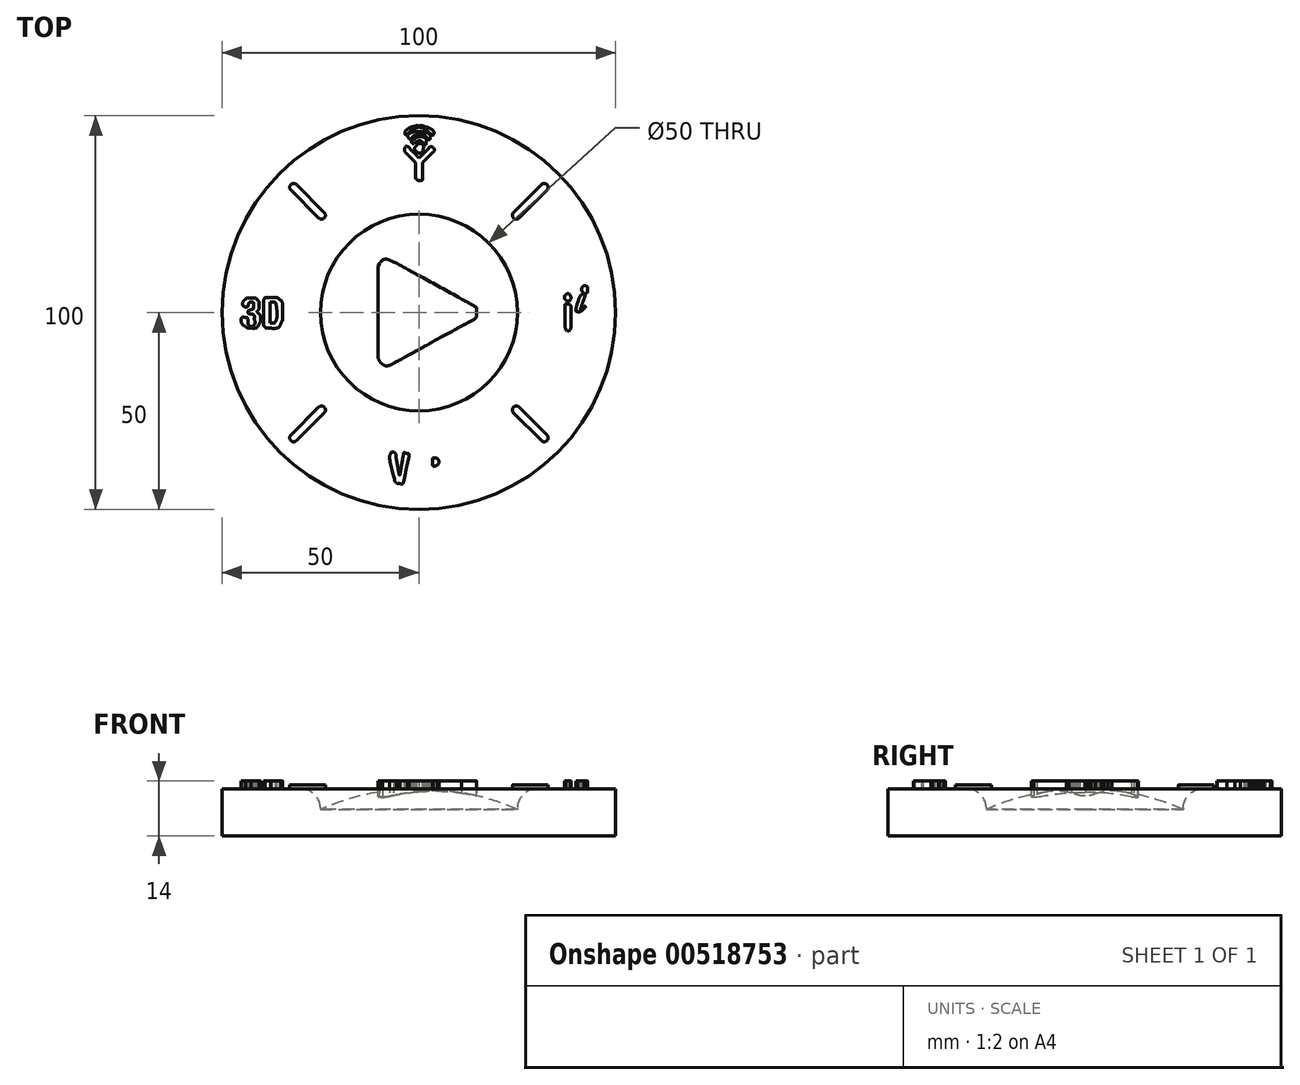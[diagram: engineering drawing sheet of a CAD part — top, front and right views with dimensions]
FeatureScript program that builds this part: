
annotation { "Feature Type Name" : "Feature", "Feature Type Description" : "" }
export const myFeature = defineFeature(function(context is Context, id is Id, definition is map)
    precondition{}
    {
        {
            var Q0;
            Q0=qCreatedBy(makeId("Top.planeOp"),FACE);
            var sketch = newSketch(context, id + "F0", { "sketchPlane" : qUnion([Q0])});
            skCircle(sketch, "E0", {"center": v(0, 0) * mm, "radius": 50 * mm});
            skCircle(sketch, "E1", {"center": v(0, 0) * mm, "radius": 25 * mm});
            skSolve(sketch);
        }
        {
            var Q0;
            Q0=makeQuery(id+"F0.imprint","IMPRINT",FACE,{"disambiguationData":[TD([[makeQuery(id+"F0.imprint","IMPRINT",EDGE,{"derivedFrom":sQuery(id+"F0.wireOp",EDGE,"E0")}),1.0]])]});
            extrude(context, id + "F1", {"entities" : qUnion([Q0]), "depth" : 25 * mm, "offsetDistance" : 25 * mm});
        }
        {
            var Q0;
            Q0=qCreatedBy(makeId("Front.planeOp"),FACE);
            var sketch = newSketch(context, id + "F2", { "sketchPlane" : qUnion([Q0])});
            skLineSegment(sketch, "E2", {"start": v(-50, 0) * mm, "end": v(50, 0) * mm});
            skLineSegment(sketch, "E3", {"start": v(0, 25) * mm, "end": v(0, 0) * mm});
            skArc(sketch, "E4", {"start": v(50, 0) * mm, "mid": v(27.95, 18.4) * mm, "end": v(0, 25) * mm});
            skLineSegment(sketch, "E5", {"start": v(0, 0) * mm, "end": v(0, -37.5) * mm});
            skSolve(sketch);
        }
        {
            var Q0;
            Q0 = qSketchRegion(id + "F2", true);
            var Q1;
            Q1=sQuery(id+"F2.wireOp",EDGE,"E3");
            revolve(context, id + "F3", {"operationType" : NewBodyOperationType.ADD, "entities" : qUnion([Q0]), "axis" : qUnion([Q1]), "revolveType" : RevolveType.FULL});
        }
        {
            var Q0;
            Q0=makeQuery(id+"F1.opExtrude","CAP_EDGE",EDGE,{"disambiguationData":[OSD([sQuery(id+"F0.wireOp",EDGE,"E1")])],"isStart":false});
            fillet(context, id + "F4", {"entities" : qUnion([Q0]), "radius" : 5 * mm, "tangentPropagation" : true, "allowEdgeOverflow" : false});
        }
        {
            var Q0;
            Q0=makeQuery(id+"F1.opExtrude","CAP_FACE",FACE,{"disambiguationData":[OSD([sQuery(id+"F0.wireOp",EDGE,"E0"),sQuery(id+"F0.wireOp",EDGE,"E1")])],"isStart":false});
            var sketch = newSketch(context, id + "F5", { "sketchPlane" : qUnion([Q0])});
            skLineSegment(sketch, "E6", {"start": v(-24.75, 24.75) * mm, "end": v(-31.82, 31.82) * mm, "construction": true});
            skLineSegment(sketch, "E7", {"start": v(24.75, -24.75) * mm, "end": v(31.82, -31.82) * mm, "construction": true});
            skLineSegment(sketch, "E8", {"start": v(31.82, 31.82) * mm, "end": v(24.75, 24.75) * mm, "construction": true});
            skLineSegment(sketch, "E9", {"start": v(-24.75, -24.75) * mm, "end": v(-31.82, -31.82) * mm, "construction": true});
            skCircle(sketch, "E10", {"center": v(0, 0) * mm, "radius": 35 * mm, "construction": true});
            skCircle(sketch, "E11", {"center": v(0, 0) * mm, "radius": 45 * mm, "construction": true});
            skArc(sketch, "E12", {"start": v(-25.46, 24.04) * mm, "mid": v(-24.04, 24.04) * mm, "end": v(-24.04, 25.46) * mm});
            skArc(sketch, "E13", {"start": v(-31.1, 32.52) * mm, "mid": v(-32.53, 32.53) * mm, "end": v(-32.52, 31.1) * mm});
            skLineSegment(sketch, "E14", {"start": v(-31.11, 32.53) * mm, "end": v(-24.04, 25.46) * mm});
            skLineSegment(sketch, "E15", {"start": v(-32.53, 31.11) * mm, "end": v(-25.46, 24.04) * mm});
            skArc(sketch, "E16", {"start": v(32.52, 31.1) * mm, "mid": v(32.53, 32.53) * mm, "end": v(31.1, 32.52) * mm});
            skArc(sketch, "E17", {"start": v(24.04, 25.46) * mm, "mid": v(24.04, 24.04) * mm, "end": v(25.46, 24.04) * mm});
            skLineSegment(sketch, "E18", {"start": v(32.53, 31.11) * mm, "end": v(25.46, 24.04) * mm});
            skLineSegment(sketch, "E19", {"start": v(31.11, 32.53) * mm, "end": v(24.04, 25.46) * mm});
            skArc(sketch, "E20", {"start": v(25.46, -24.04) * mm, "mid": v(24.04, -24.04) * mm, "end": v(24.04, -25.46) * mm});
            skArc(sketch, "E21", {"start": v(31.1, -32.52) * mm, "mid": v(32.53, -32.53) * mm, "end": v(32.52, -31.1) * mm});
            skLineSegment(sketch, "E22", {"start": v(25.46, -24.04) * mm, "end": v(32.53, -31.11) * mm});
            skLineSegment(sketch, "E23", {"start": v(24.04, -25.46) * mm, "end": v(31.11, -32.53) * mm});
            skArc(sketch, "E24", {"start": v(-24.04, -25.46) * mm, "mid": v(-24.04, -24.04) * mm, "end": v(-25.46, -24.04) * mm});
            skArc(sketch, "E25", {"start": v(-32.52, -31.1) * mm, "mid": v(-32.53, -32.53) * mm, "end": v(-31.1, -32.52) * mm});
            skLineSegment(sketch, "E26", {"start": v(-32.53, -31.11) * mm, "end": v(-25.46, -24.04) * mm});
            skLineSegment(sketch, "E27", {"start": v(-24.04, -25.46) * mm, "end": v(-31.11, -32.53) * mm});
            skSolve(sketch);
        }
        {
            var Q0;
            Q0 = qSketchRegion(id + "F5", true);
            extrude(context, id + "F6", {"entities" : qUnion([Q0]), "operationType" : NewBodyOperationType.ADD, "depth" : 1 * mm, "offsetDistance" : 25 * mm});
        }
        {
            var Q0;
            Q0=makeQuery(id+"F1.opExtrude","CAP_FACE",FACE,{"disambiguationData":[OSD([sQuery(id+"F0.wireOp",EDGE,"E0"),sQuery(id+"F0.wireOp",EDGE,"E1")])],"isStart":false});
            var sketch = newSketch(context, id + "F7", { "sketchPlane" : qUnion([Q0])});
            skFitSpline(sketch, "E28", {"points": [v(-1.16, -44.63) * mm, v(-1.22, -44.57) * mm, v(-1.27, -44.21) * mm, v(-1.27, -43.84) * mm]});
            skFitSpline(sketch, "E29", {"points": [v(-1.98, -43.15) * mm, v(-2.6, -43.15) * mm, v(-2.7, -43.1) * mm, v(-2.7, -42.83) * mm]});
            skFitSpline(sketch, "E30", {"points": [v(-2.7, -42.83) * mm, v(-2.7, -42.56) * mm, v(-2.6, -42.51) * mm, v(-2, -42.51) * mm]});
            skLineSegment(sketch, "E31", {"start": v(-1.27, -43.84) * mm, "end": v(-1.27, -43.15) * mm});
            skLineSegment(sketch, "E32", {"start": v(-1.27, -43.15) * mm, "end": v(-1.98, -43.15) * mm});
            skFitSpline(sketch, "E33", {"points": [v(-1.24, -41.76) * mm, v(-1.2, -41.13) * mm, v(-1.14, -41) * mm, v(-0.87, -41) * mm]});
            skFitSpline(sketch, "E34", {"points": [v(-0.87, -41) * mm, v(-0.6, -41) * mm, v(-0.55, -41.13) * mm, v(-0.5, -41.76) * mm]});
            skLineSegment(sketch, "E35", {"start": v(-2, -42.51) * mm, "end": v(-1.28, -42.51) * mm});
            skLineSegment(sketch, "E36", {"start": v(-1.28, -42.51) * mm, "end": v(-1.24, -41.76) * mm});
            skFitSpline(sketch, "E37", {"points": [v(0.25, -42.51) * mm, v(0.85, -42.51) * mm, v(0.95, -42.56) * mm, v(0.95, -42.83) * mm]});
            skFitSpline(sketch, "E38", {"points": [v(0.95, -42.83) * mm, v(0.95, -43.1) * mm, v(0.85, -43.15) * mm, v(0.24, -43.15) * mm]});
            skLineSegment(sketch, "E39", {"start": v(-0.5, -41.76) * mm, "end": v(-0.46, -42.51) * mm});
            skLineSegment(sketch, "E40", {"start": v(-0.46, -42.51) * mm, "end": v(0.25, -42.51) * mm});
            skFitSpline(sketch, "E41", {"points": [v(-0.47, -43.84) * mm, v(-0.47, -44.33) * mm, v(-0.55, -44.57) * mm, v(-0.72, -44.64) * mm]});
            skFitSpline(sketch, "E42", {"points": [v(-0.72, -44.64) * mm, v(-1.04, -44.76) * mm, v(-1.03, -44.76) * mm, v(-1.16, -44.63) * mm]});
            skLineSegment(sketch, "E43", {"start": v(0.24, -43.15) * mm, "end": v(-0.47, -43.15) * mm});
            skLineSegment(sketch, "E44", {"start": v(-0.47, -43.15) * mm, "end": v(-0.47, -43.84) * mm});
            skFitSpline(sketch, "E45", {"points": [v(-5.73, -43.2) * mm, v(-6.06, -42.81) * mm, v(-7.46, -36.46) * mm, v(-7.29, -36.14) * mm]});
            skFitSpline(sketch, "E46", {"points": [v(-7.29, -36.14) * mm, v(-6.91, -35.44) * mm, v(-5.98, -35.78) * mm, v(-5.82, -36.67) * mm]});
            skFitSpline(sketch, "E47", {"points": [v(-5.82, -36.67) * mm, v(-5.43, -38.9) * mm, v(-5.05, -40.9) * mm, v(-4.96, -41.16) * mm]});
            skFitSpline(sketch, "E48", {"points": [v(-4.96, -41.16) * mm, v(-4.9, -41.35) * mm, v(-4.71, -40.6) * mm, v(-4.49, -39.26) * mm]});
            skFitSpline(sketch, "E49", {"points": [v(-4.49, -39.26) * mm, v(-3.9, -35.79) * mm, v(-3.82, -35.59) * mm, v(-3.03, -35.8) * mm]});
            skFitSpline(sketch, "E50", {"points": [v(-3.03, -35.8) * mm, v(-2.53, -35.93) * mm, v(-2.49, -36.41) * mm, v(-2.84, -38) * mm]});
            skFitSpline(sketch, "E51", {"points": [v(-2.84, -38) * mm, v(-3.01, -38.78) * mm, v(-3.3, -40.17) * mm, v(-3.5, -41.08) * mm]});
            skFitSpline(sketch, "E52", {"points": [v(-3.5, -41.08) * mm, v(-3.92, -43.17) * mm, v(-4.1, -43.46) * mm, v(-4.9, -43.46) * mm]});
            skFitSpline(sketch, "E53", {"points": [v(-4.9, -43.46) * mm, v(-5.28, -43.46) * mm, v(-5.6, -43.36) * mm, v(-5.73, -43.2) * mm]});
            skFitSpline(sketch, "E54", {"points": [v(2.26, -43.27) * mm, v(2.12, -43.14) * mm, v(2.07, -42.09) * mm, v(2.07, -39.55) * mm]});
            skFitSpline(sketch, "E55", {"points": [v(2.07, -39.55) * mm, v(2.07, -35.44) * mm, v(1.95, -35.69) * mm, v(3.84, -35.69) * mm]});
            skFitSpline(sketch, "E56", {"points": [v(3.84, -35.69) * mm, v(5.74, -35.69) * mm, v(6.5, -36.27) * mm, v(6.5, -37.72) * mm]});
            skFitSpline(sketch, "E57", {"points": [v(6.5, -37.72) * mm, v(6.51, -38.45) * mm, v(6.14, -39.34) * mm, v(5.84, -39.34) * mm]});
            skFitSpline(sketch, "E58", {"points": [v(5.84, -39.34) * mm, v(5.74, -39.34) * mm, v(5.81, -39.48) * mm, v(6, -39.66) * mm]});
            skFitSpline(sketch, "E59", {"points": [v(6, -39.66) * mm, v(6.46, -40.09) * mm, v(6.53, -40.44) * mm, v(6.48, -42.04) * mm]});
            skFitSpline(sketch, "E60", {"points": [v(5.88, -43.44) * mm, v(5.12, -43.5) * mm, v(4.92, -43.18) * mm, v(4.92, -41.84) * mm]});
            skFitSpline(sketch, "E61", {"points": [v(4.92, -41.84) * mm, v(4.92, -40.45) * mm, v(4.76, -40.13) * mm, v(4.04, -40.13) * mm]});
            skLineSegment(sketch, "E62", {"start": v(6.48, -42.04) * mm, "end": v(6.43, -43.39) * mm});
            skLineSegment(sketch, "E63", {"start": v(6.43, -43.39) * mm, "end": v(5.88, -43.44) * mm});
            skFitSpline(sketch, "E64", {"points": [v(3.5, -41.6) * mm, v(3.5, -43.16) * mm, v(3.38, -43.46) * mm, v(2.78, -43.46) * mm]});
            skFitSpline(sketch, "E65", {"points": [v(2.78, -43.46) * mm, v(2.6, -43.46) * mm, v(2.36, -43.38) * mm, v(2.26, -43.27) * mm]});
            skLineSegment(sketch, "E66", {"start": v(4.04, -40.13) * mm, "end": v(3.5, -40.13) * mm});
            skLineSegment(sketch, "E67", {"start": v(3.5, -40.13) * mm, "end": v(3.5, -41.6) * mm});
            skFitSpline(sketch, "E68", {"points": [v(4.72, -38.66) * mm, v(4.98, -38.46) * mm, v(4.98, -37.4) * mm, v(4.73, -37.15) * mm]});
            skFitSpline(sketch, "E69", {"points": [v(4.73, -37.15) * mm, v(4.63, -37.04) * mm, v(4.3, -36.96) * mm, v(4.02, -36.96) * mm]});
            skFitSpline(sketch, "E70", {"points": [v(3.5, -37.88) * mm, v(3.5, -38.4) * mm, v(3.54, -38.86) * mm, v(3.6, -38.91) * mm]});
            skFitSpline(sketch, "E71", {"points": [v(3.6, -38.91) * mm, v(3.72, -39.04) * mm, v(4.45, -38.88) * mm, v(4.72, -38.66) * mm]});
            skLineSegment(sketch, "E72", {"start": v(4.02, -36.96) * mm, "end": v(3.5, -36.96) * mm});
            skLineSegment(sketch, "E73", {"start": v(3.5, -36.96) * mm, "end": v(3.5, -37.88) * mm});
            skFitSpline(sketch, "E74", {"points": [v(-9.29, -13.06) * mm, v(-9.56, -12.9) * mm, v(-9.91, -12.49) * mm, v(-10.08, -12.15) * mm]});
            skFitSpline(sketch, "E75", {"points": [v(-10.08, -12.15) * mm, v(-10.37, -11.56) * mm, v(-10.39, -11.05) * mm, v(-10.39, 0.14) * mm]});
            skFitSpline(sketch, "E76", {"points": [v(-9.95, 12.48) * mm, v(-9.52, 13.12) * mm, v(-8.57, 13.59) * mm, v(-7.48, 13.3) * mm]});
            skFitSpline(sketch, "E77", {"points": [v(-7.48, 13.3) * mm, v(-7.08, 13.21) * mm, v(-3.83, 11.51) * mm, v(-0.24, 9.54) * mm]});
            skFitSpline(sketch, "E78", {"points": [v(-0.24, 9.54) * mm, v(3.35, 7.57) * mm, v(7.89, 5.07) * mm, v(9.85, 4) * mm]});
            skFitSpline(sketch, "E79", {"points": [v(9.85, 4) * mm, v(13.83, 1.81) * mm, v(14.61, 1.19) * mm, v(14.61, 0.2) * mm]});
            skFitSpline(sketch, "E80", {"points": [v(14.61, 0.2) * mm, v(14.61, -1.08) * mm, v(13.93, -1.73) * mm, v(10.8, -3.44) * mm]});
            skFitSpline(sketch, "E81", {"points": [v(10.8, -3.44) * mm, v(9.53, -4.12) * mm, v(5.34, -6.42) * mm, v(1.47, -8.55) * mm]});
            skFitSpline(sketch, "E82", {"points": [v(1.47, -8.55) * mm, v(-2.4, -10.68) * mm, v(-5.98, -12.63) * mm, v(-6.49, -12.9) * mm]});
            skFitSpline(sketch, "E83", {"points": [v(-6.49, -12.9) * mm, v(-7.58, -13.45) * mm, v(-8.56, -13.5) * mm, v(-9.29, -13.06) * mm]});
            skLineSegment(sketch, "E84", {"start": v(-10.39, 0.14) * mm, "end": v(-10.39, 11.82) * mm});
            skLineSegment(sketch, "E85", {"start": v(-10.39, 11.82) * mm, "end": v(-9.95, 12.48) * mm});
            skFitSpline(sketch, "E86", {"points": [v(-4.77, -10.48) * mm, v(-3.32, -9.68) * mm, v(-1.77, -8.84) * mm, v(-1.34, -8.6) * mm]});
            skFitSpline(sketch, "E87", {"points": [v(-1.34, -8.6) * mm, v(-0.9, -8.36) * mm, v(2.35, -6.58) * mm, v(5.88, -4.64) * mm]});
            skFitSpline(sketch, "E88", {"points": [v(5.88, -4.64) * mm, v(9.5, -2.67) * mm, v(12.5, -0.91) * mm, v(12.75, -0.65) * mm]});
            skFitSpline(sketch, "E89", {"points": [v(12.75, -0.65) * mm, v(13.28, -0.08) * mm, v(13.3, 0.29) * mm, v(12.83, 0.72) * mm]});
            skFitSpline(sketch, "E90", {"points": [v(12.83, 0.72) * mm, v(12.63, 0.9) * mm, v(10.3, 2.25) * mm, v(7.63, 3.7) * mm]});
            skFitSpline(sketch, "E91", {"points": [v(7.63, 3.7) * mm, v(4.97, 5.16) * mm, v(0.53, 7.6) * mm, v(-2.23, 9.12) * mm]});
            skFitSpline(sketch, "E92", {"points": [v(-2.23, 9.12) * mm, v(-6.44, 11.43) * mm, v(-7.35, 11.88) * mm, v(-7.9, 11.88) * mm]});
            skFitSpline(sketch, "E93", {"points": [v(-7.9, 11.88) * mm, v(-9.1, 11.88) * mm, v(-9.05, 12.42) * mm, v(-9, -0.07) * mm]});
            skFitSpline(sketch, "E94", {"points": [v(-9, -0.07) * mm, v(-8.96, -10.3) * mm, v(-8.94, -11.1) * mm, v(-8.68, -11.5) * mm]});
            skFitSpline(sketch, "E95", {"points": [v(-8.68, -11.5) * mm, v(-8.2, -12.22) * mm, v(-7.69, -12.09) * mm, v(-4.77, -10.48) * mm]});
            skFitSpline(sketch, "E96", {"points": [v(37.23, -3.98) * mm, v(37.14, -3.75) * mm, v(37.07, -2.47) * mm, v(37.07, -1.13) * mm]});
            skFitSpline(sketch, "E97", {"points": [v(37.07, -1.13) * mm, v(37.07, 1.7) * mm, v(37.18, 2.12) * mm, v(37.86, 2.12) * mm]});
            skFitSpline(sketch, "E98", {"points": [v(37.86, 2.12) * mm, v(38.17, 2.12) * mm, v(38.4, 2.01) * mm, v(38.5, 1.82) * mm]});
            skFitSpline(sketch, "E99", {"points": [v(38.5, 1.82) * mm, v(38.6, 1.64) * mm, v(38.66, 0.39) * mm, v(38.66, -1.13) * mm]});
            skFitSpline(sketch, "E100", {"points": [v(38.66, -1.13) * mm, v(38.66, -2.65) * mm, v(38.6, -3.9) * mm, v(38.5, -4.08) * mm]});
            skFitSpline(sketch, "E101", {"points": [v(38.5, -4.08) * mm, v(38.24, -4.56) * mm, v(37.43, -4.5) * mm, v(37.23, -3.98) * mm]});
            skFitSpline(sketch, "E102", {"points": [v(-44.03, -3.56) * mm, v(-44.99, -2.75) * mm, v(-45, -1.27) * mm, v(-44.06, -1.27) * mm]});
            skFitSpline(sketch, "E103", {"points": [v(-44.06, -1.27) * mm, v(-43.62, -1.27) * mm, v(-43.56, -1.33) * mm, v(-43.4, -1.98) * mm]});
            skFitSpline(sketch, "E104", {"points": [v(-43.4, -1.98) * mm, v(-43.01, -3.51) * mm, v(-41.83, -3.16) * mm, v(-41.83, -1.52) * mm]});
            skFitSpline(sketch, "E105", {"points": [v(-41.83, -1.52) * mm, v(-41.83, -0.84) * mm, v(-42.12, -0.47) * mm, v(-42.79, -0.33) * mm]});
            skFitSpline(sketch, "E106", {"points": [v(-42.79, -0.33) * mm, v(-43.23, -0.24) * mm, v(-43.33, -0.15) * mm, v(-43.33, 0.16) * mm]});
            skFitSpline(sketch, "E107", {"points": [v(-43.33, 0.16) * mm, v(-43.33, 0.44) * mm, v(-43.21, 0.57) * mm, v(-42.86, 0.69) * mm]});
            skFitSpline(sketch, "E108", {"points": [v(-42.86, 0.69) * mm, v(-42.14, 0.92) * mm, v(-41.99, 1.1) * mm, v(-41.99, 1.74) * mm]});
            skFitSpline(sketch, "E109", {"points": [v(-41.99, 1.74) * mm, v(-41.99, 2.4) * mm, v(-42.21, 2.7) * mm, v(-42.7, 2.7) * mm]});
            skFitSpline(sketch, "E110", {"points": [v(-42.7, 2.7) * mm, v(-42.96, 2.7) * mm, v(-43.11, 2.53) * mm, v(-43.3, 2.07) * mm]});
            skFitSpline(sketch, "E111", {"points": [v(-43.3, 2.07) * mm, v(-43.5, 1.57) * mm, v(-43.63, 1.43) * mm, v(-43.94, 1.43) * mm]});
            skFitSpline(sketch, "E112", {"points": [v(-43.94, 1.43) * mm, v(-44.15, 1.43) * mm, v(-44.42, 1.54) * mm, v(-44.52, 1.67) * mm]});
            skFitSpline(sketch, "E113", {"points": [v(-44.52, 1.67) * mm, v(-44.81, 2.01) * mm, v(-44.6, 2.9) * mm, v(-44.11, 3.35) * mm]});
            skFitSpline(sketch, "E114", {"points": [v(-44.11, 3.35) * mm, v(-43.76, 3.68) * mm, v(-43.55, 3.73) * mm, v(-42.6, 3.73) * mm]});
            skFitSpline(sketch, "E115", {"points": [v(-42.6, 3.73) * mm, v(-41.54, 3.73) * mm, v(-41.46, 3.7) * mm, v(-41.02, 3.22) * mm]});
            skFitSpline(sketch, "E116", {"points": [v(-41.02, 3.22) * mm, v(-40.63, 2.78) * mm, v(-40.56, 2.56) * mm, v(-40.56, 1.85) * mm]});
            skFitSpline(sketch, "E117", {"points": [v(-40.56, 1.85) * mm, v(-40.56, 1.24) * mm, v(-40.65, 0.88) * mm, v(-40.86, 0.62) * mm]});
            skFitSpline(sketch, "E118", {"points": [v(-40.86, 0.62) * mm, v(-41.17, 0.25) * mm, v(-41.16, 0.24) * mm, v(-40.83, -0.12) * mm]});
            skFitSpline(sketch, "E119", {"points": [v(-40.83, -0.12) * mm, v(-40.36, -0.63) * mm, v(-40.27, -2.23) * mm, v(-40.67, -3) * mm]});
            skFitSpline(sketch, "E120", {"points": [v(-40.67, -3) * mm, v(-41.04, -3.72) * mm, v(-41.53, -3.96) * mm, v(-42.65, -3.96) * mm]});
            skFitSpline(sketch, "E121", {"points": [v(-42.65, -3.96) * mm, v(-43.39, -3.96) * mm, v(-43.64, -3.89) * mm, v(-44.03, -3.56) * mm]});
            skFitSpline(sketch, "E122", {"points": [v(-39.13, -3.65) * mm, v(-39.43, -3.35) * mm, v(-39.45, -3.12) * mm, v(-39.45, -0.06) * mm]});
            skFitSpline(sketch, "E123", {"points": [v(-39.45, -0.06) * mm, v(-39.45, 1.88) * mm, v(-39.38, 3.32) * mm, v(-39.28, 3.5) * mm]});
            skFitSpline(sketch, "E124", {"points": [v(-39.28, 3.5) * mm, v(-39.14, 3.78) * mm, v(-38.94, 3.81) * mm, v(-37.55, 3.81) * mm]});
            skFitSpline(sketch, "E125", {"points": [v(-37.55, 3.81) * mm, v(-36.1, 3.81) * mm, v(-35.94, 3.78) * mm, v(-35.5, 3.4) * mm]});
            skFitSpline(sketch, "E126", {"points": [v(-35.5, 3.4) * mm, v(-34.84, 2.85) * mm, v(-34.63, 2.02) * mm, v(-34.63, -0.09) * mm]});
            skFitSpline(sketch, "E127", {"points": [v(-34.63, -0.09) * mm, v(-34.62, -1.64) * mm, v(-34.67, -1.94) * mm, v(-35.01, -2.63) * mm]});
            skFitSpline(sketch, "E128", {"points": [v(-35.01, -2.63) * mm, v(-35.52, -3.66) * mm, v(-36.13, -3.96) * mm, v(-37.66, -3.96) * mm]});
            skFitSpline(sketch, "E129", {"points": [v(-37.66, -3.96) * mm, v(-38.6, -3.96) * mm, v(-38.87, -3.9) * mm, v(-39.13, -3.65) * mm]});
            skFitSpline(sketch, "E130", {"points": [v(-36.52, -2.33) * mm, v(-36.22, -1.87) * mm, v(-36.04, 0.01) * mm, v(-36.18, 1.19) * mm]});
            skFitSpline(sketch, "E131", {"points": [v(-36.18, 1.19) * mm, v(-36.32, 2.24) * mm, v(-36.68, 2.7) * mm, v(-37.38, 2.7) * mm]});
            skFitSpline(sketch, "E132", {"points": [v(-37.3, -2.7) * mm, v(-36.9, -2.7) * mm, v(-36.69, -2.6) * mm, v(-36.52, -2.33) * mm]});
            skLineSegment(sketch, "E133", {"start": v(-37.38, 2.7) * mm, "end": v(-37.86, 2.7) * mm});
            skLineSegment(sketch, "E134", {"start": v(-37.86, 2.7) * mm, "end": v(-37.86, 0) * mm});
            skLineSegment(sketch, "E135", {"start": v(-37.86, 0) * mm, "end": v(-37.86, -2.7) * mm});
            skLineSegment(sketch, "E136", {"start": v(-37.86, -2.7) * mm, "end": v(-37.3, -2.7) * mm});
            skFitSpline(sketch, "E137", {"points": [v(39.93, 0.58) * mm, v(39.93, 1.1) * mm, v(41.03, 4.3) * mm, v(41.28, 4.5) * mm]});
            skFitSpline(sketch, "E138", {"points": [v(41.28, 4.5) * mm, v(41.5, 4.7) * mm, v(42.15, 4.47) * mm, v(42.15, 4.2) * mm]});
            skFitSpline(sketch, "E139", {"points": [v(42.15, 4.2) * mm, v(42.15, 4.14) * mm, v(41.94, 3.46) * mm, v(41.68, 2.7) * mm]});
            skFitSpline(sketch, "E140", {"points": [v(41.68, 2.7) * mm, v(41.07, 0.96) * mm, v(41.06, 0.66) * mm, v(41.6, 1.17) * mm]});
            skFitSpline(sketch, "E141", {"points": [v(41.6, 1.17) * mm, v(42.07, 1.62) * mm, v(42.33, 1.47) * mm, v(41.9, 1) * mm]});
            skFitSpline(sketch, "E142", {"points": [v(41.9, 1) * mm, v(41.5, 0.55) * mm, v(40.83, 0.22) * mm, v(40.34, 0.22) * mm]});
            skFitSpline(sketch, "E143", {"points": [v(40.34, 0.22) * mm, v(40.02, 0.22) * mm, v(39.93, 0.3) * mm, v(39.93, 0.58) * mm]});
            skFitSpline(sketch, "E144", {"points": [v(37.27, 3.26) * mm, v(37, 3.53) * mm, v(37.01, 4.21) * mm, v(37.3, 4.5) * mm]});
            skFitSpline(sketch, "E145", {"points": [v(37.3, 4.5) * mm, v(37.63, 4.77) * mm, v(38.22, 4.7) * mm, v(38.47, 4.34) * mm]});
            skFitSpline(sketch, "E146", {"points": [v(38.47, 4.34) * mm, v(38.57, 4.1) * mm, v(38.66, 3.75) * mm, v(38.5, 3.43) * mm]});
            skFitSpline(sketch, "E147", {"points": [v(38.5, 3.43) * mm, v(38.28, 2.98) * mm, v(37.6, 2.93) * mm, v(37.27, 3.26) * mm]});
            skFitSpline(sketch, "E148", {"points": [v(41.45, 5.49) * mm, v(41.24, 5.79) * mm, v(41.24, 5.89) * mm, v(41.42, 6.16) * mm]});
            skFitSpline(sketch, "E149", {"points": [v(41.42, 6.16) * mm, v(41.84, 6.8) * mm, v(42.79, 6.6) * mm, v(42.79, 5.87) * mm]});
            skFitSpline(sketch, "E150", {"points": [v(42.79, 5.87) * mm, v(42.79, 5.12) * mm, v(41.89, 4.87) * mm, v(41.45, 5.49) * mm]});
            skFitSpline(sketch, "E151", {"points": [v(-0.56, 33.85) * mm, v(-0.76, 34.05) * mm, v(-0.81, 34.5) * mm, v(-0.81, 36.12) * mm]});
            skFitSpline(sketch, "E152", {"points": [v(-2.24, 39.56) * mm, v(-3.14, 40.45) * mm, v(-3.67, 41.1) * mm, v(-3.67, 41.31) * mm]});
            skFitSpline(sketch, "E153", {"points": [v(-3.67, 41.31) * mm, v(-3.67, 41.64) * mm, v(-3.21, 42.26) * mm, v(-2.96, 42.17) * mm]});
            skFitSpline(sketch, "E154", {"points": [v(-2.96, 42.17) * mm, v(-2.54, 42.03) * mm, v(-2.18, 41.53) * mm, v(-1.38, 40.75) * mm]});
            skLineSegment(sketch, "E155", {"start": v(-0.81, 36.12) * mm, "end": v(-0.81, 38.13) * mm});
            skLineSegment(sketch, "E156", {"start": v(-0.81, 38.13) * mm, "end": v(-2.24, 39.56) * mm});
            skFitSpline(sketch, "E157", {"points": [v(1.41, 40.67) * mm, v(2.74, 42) * mm, v(3.19, 42.24) * mm, v(3.6, 41.83) * mm]});
            skFitSpline(sketch, "E158", {"points": [v(3.6, 41.83) * mm, v(4.02, 41.4) * mm, v(3.77, 40.96) * mm, v(2.36, 39.56) * mm]});
            skLineSegment(sketch, "E159", {"start": v(-1.38, 40.75) * mm, "end": v(0.07, 39.32) * mm});
            skLineSegment(sketch, "E160", {"start": v(0.07, 39.32) * mm, "end": v(1.41, 40.67) * mm});
            skFitSpline(sketch, "E161", {"points": [v(0.93, 36.12) * mm, v(0.93, 33.93) * mm, v(0.82, 33.6) * mm, v(0.06, 33.6) * mm]});
            skFitSpline(sketch, "E162", {"points": [v(0.06, 33.6) * mm, v(-0.14, 33.6) * mm, v(-0.43, 33.72) * mm, v(-0.56, 33.85) * mm]});
            skLineSegment(sketch, "E163", {"start": v(2.36, 39.56) * mm, "end": v(0.93, 38.13) * mm});
            skLineSegment(sketch, "E164", {"start": v(0.93, 38.13) * mm, "end": v(0.93, 36.12) * mm});
            skFitSpline(sketch, "E165", {"points": [v(-0.63, 40.95) * mm, v(-1.06, 41.41) * mm, v(-1.07, 41.92) * mm, v(-0.65, 42.33) * mm]});
            skFitSpline(sketch, "E166", {"points": [v(-0.65, 42.33) * mm, v(-0.04, 42.95) * mm, v(1.1, 42.5) * mm, v(1.1, 41.65) * mm]});
            skFitSpline(sketch, "E167", {"points": [v(1.1, 41.65) * mm, v(1.1, 41.17) * mm, v(0.54, 40.59) * mm, v(0.08, 40.59) * mm]});
            skFitSpline(sketch, "E168", {"points": [v(0.08, 40.59) * mm, v(-0.12, 40.59) * mm, v(-0.44, 40.75) * mm, v(-0.63, 40.95) * mm]});
            skFitSpline(sketch, "E169", {"points": [v(1.1, 43.12) * mm, v(0.44, 43.63) * mm, v(-0.1, 43.67) * mm, v(-0.81, 43.27) * mm]});
            skFitSpline(sketch, "E170", {"points": [v(-0.81, 43.27) * mm, v(-1.28, 43) * mm, v(-1.5, 42.95) * mm, v(-1.63, 43.09) * mm]});
            skFitSpline(sketch, "E171", {"points": [v(-1.63, 43.09) * mm, v(-1.89, 43.34) * mm, v(-1.7, 43.71) * mm, v(-1.1, 44.09) * mm]});
            skFitSpline(sketch, "E172", {"points": [v(-1.1, 44.09) * mm, v(-0.1, 44.71) * mm, v(1.8, 44.18) * mm, v(1.8, 43.28) * mm]});
            skFitSpline(sketch, "E173", {"points": [v(1.8, 43.28) * mm, v(1.8, 42.8) * mm, v(1.58, 42.75) * mm, v(1.1, 43.12) * mm]});
            skFitSpline(sketch, "E174", {"points": [v(2.04, 44.33) * mm, v(1.37, 45.14) * mm, v(-0.66, 45.28) * mm, v(-1.6, 44.59) * mm]});
            skFitSpline(sketch, "E175", {"points": [v(-1.6, 44.59) * mm, v(-2.15, 44.18) * mm, v(-2.49, 44.14) * mm, v(-2.62, 44.49) * mm]});
            skFitSpline(sketch, "E176", {"points": [v(-2.62, 44.49) * mm, v(-2.83, 45.04) * mm, v(-1.13, 45.98) * mm, v(0.07, 45.98) * mm]});
            skFitSpline(sketch, "E177", {"points": [v(0.07, 45.98) * mm, v(1.25, 45.98) * mm, v(2.84, 45.11) * mm, v(2.84, 44.47) * mm]});
            skFitSpline(sketch, "E178", {"points": [v(2.84, 44.47) * mm, v(2.84, 44.01) * mm, v(2.37, 43.93) * mm, v(2.04, 44.33) * mm]});
            skFitSpline(sketch, "E179", {"points": [v(2.56, 45.75) * mm, v(1.1, 46.9) * mm, v(-0.98, 46.9) * mm, v(-2.5, 45.74) * mm]});
            skFitSpline(sketch, "E180", {"points": [v(-2.5, 45.74) * mm, v(-3.04, 45.33) * mm, v(-3.56, 45.36) * mm, v(-3.48, 45.8) * mm]});
            skFitSpline(sketch, "E181", {"points": [v(-3.48, 45.8) * mm, v(-3.4, 46.17) * mm, v(-2.16, 47.06) * mm, v(-1.4, 47.28) * mm]});
            skFitSpline(sketch, "E182", {"points": [v(-1.4, 47.28) * mm, v(-0.44, 47.55) * mm, v(0.73, 47.52) * mm, v(1.68, 47.2) * mm]});
            skFitSpline(sketch, "E183", {"points": [v(1.68, 47.2) * mm, v(2.7, 46.85) * mm, v(3.9, 45.84) * mm, v(3.74, 45.46) * mm]});
            skFitSpline(sketch, "E184", {"points": [v(3.74, 45.46) * mm, v(3.6, 45.08) * mm, v(3.18, 45.27) * mm, v(2.56, 45.75) * mm]});
            skSolve(sketch);
        }
        {
            var Q0;
            Q0 = qSketchRegion(id + "F7", true);
            extrude(context, id + "F8", {"entities" : qUnion([Q0]), "operationType" : NewBodyOperationType.ADD, "depth" : 2 * mm, "offsetDistance" : 25 * mm});
        }
        {
            var Q0;
            Q0=makeQuery(id+"F8.opExtrude","CAP_FACE",FACE,{"disambiguationData":[OSD([sQuery(id+"F7.wireOp",EDGE,"E74"),sQuery(id+"F7.wireOp",EDGE,"E75"),sQuery(id+"F7.wireOp",EDGE,"E76"),sQuery(id+"F7.wireOp",EDGE,"E77"),sQuery(id+"F7.wireOp",EDGE,"E78"),sQuery(id+"F7.wireOp",EDGE,"E79"),sQuery(id+"F7.wireOp",EDGE,"E80"),sQuery(id+"F7.wireOp",EDGE,"E81"),sQuery(id+"F7.wireOp",EDGE,"E82"),sQuery(id+"F7.wireOp",EDGE,"E83"),sQuery(id+"F7.wireOp",EDGE,"E84"),sQuery(id+"F7.wireOp",EDGE,"E85"),sQuery(id+"F7.wireOp",EDGE,"E86"),sQuery(id+"F7.wireOp",EDGE,"E87"),sQuery(id+"F7.wireOp",EDGE,"E88"),sQuery(id+"F7.wireOp",EDGE,"E89"),sQuery(id+"F7.wireOp",EDGE,"E90"),sQuery(id+"F7.wireOp",EDGE,"E91"),sQuery(id+"F7.wireOp",EDGE,"E92"),sQuery(id+"F7.wireOp",EDGE,"E93"),sQuery(id+"F7.wireOp",EDGE,"E94"),sQuery(id+"F7.wireOp",EDGE,"E95")])],"isStart":false});
            var Q1;
            Q1=sQuery(id+"F7.wireOp",EDGE,"E87");
            var Q2;
            Q2=sQuery(id+"F7.wireOp",EDGE,"E78");
            var Q3;
            Q3=sQuery(id+"F7.wireOp",EDGE,"E77");
            var Q4;
            Q4=sQuery(id+"F7.wireOp",EDGE,"E88");
            var Q5;
            Q5=sQuery(id+"F7.wireOp",EDGE,"E91");
            var Q6;
            Q6=sQuery(id+"F7.wireOp",EDGE,"E93");
            var Q7;
            Q7=sQuery(id+"F7.wireOp",EDGE,"E75");
            var Q8;
            Q8=sQuery(id+"F7.wireOp",EDGE,"E82");
            var Q9;
            Q9=sQuery(id+"F7.wireOp",EDGE,"E95");
            var Q10;
            Q10=sQuery(id+"F7.wireOp",EDGE,"E90");
            var Q11;
            Q11=sQuery(id+"F7.wireOp",EDGE,"E94");
            var Q12;
            Q12=sQuery(id+"F7.wireOp",EDGE,"E83");
            var Q13;
            Q13=sQuery(id+"F7.wireOp",EDGE,"E92");
            var Q14;
            Q14=sQuery(id+"F7.wireOp",EDGE,"E81");
            var Q15;
            Q15=sQuery(id+"F7.wireOp",EDGE,"E86");
            var Q16;
            Q16=sQuery(id+"F7.wireOp",EDGE,"E79");
            var Q17;
            Q17=sQuery(id+"F7.wireOp",EDGE,"E80");
            var Q18;
            Q18=sQuery(id+"F7.wireOp",EDGE,"E84");
            var Q19;
            Q19=sQuery(id+"F7.wireOp",EDGE,"E85");
            var Q20;
            Q20=sQuery(id+"F7.wireOp",EDGE,"E74");
            var Q21;
            Q21=sQuery(id+"F7.wireOp",EDGE,"E89");
            var Q22;
            Q22=sQuery(id+"F7.wireOp",EDGE,"E76");
            extrude(context, id + "F9", {"entities" : qUnion([Q0]), "operationType" : NewBodyOperationType.ADD, "surfaceEntities" : qUnion([Q1, Q2, Q3, Q4, Q5, Q6, Q7, Q8, Q9, Q10, Q11, Q12, Q13, Q14, Q15, Q16, Q17, Q18, Q19, Q20, Q21, Q22]), "oppositeDirection" : true, "depth" : 10 * mm, "offsetDistance" : 25 * mm});
        }
        {
            var Q0;
            Q0=makeQuery(id+"F3.boolean.opBoolean","MERGE",FACE,{"derivedFrom":[makeQuery(id+"F1.opExtrude","CAP_FACE",FACE,{"disambiguationData":[OSD([sQuery(id+"F0.wireOp",EDGE,"E0"),sQuery(id+"F0.wireOp",EDGE,"E1")])],"isStart":true}),makeQuery(id+"F3.opRevolve","SWEPT_FACE",FACE,{"disambiguationData":[OSD([sQuery(id+"F2.wireOp",EDGE,"E2")])]})]});
            extrude(context, id + "F10", {"entities" : qUnion([Q0]), "operationType" : NewBodyOperationType.REMOVE, "oppositeDirection" : true, "depth" : 5 * mm, "offsetDistance" : 25 * mm});
        }
        {
            var Q0;
            Q0=makeQuery(id+"F10.boolean.opBoolean","COPY",FACE,{"derivedFrom":makeQuery(id+"F10.opExtrude","CAP_FACE",FACE,{"disambiguationData":[OSD([sQuery(id+"F0.wireOp",EDGE,"E0"),sQuery(id+"F0.wireOp",EDGE,"E1"),sQuery(id+"F2.wireOp",EDGE,"E2")])],"isStart":false})});
            extrude(context, id + "F11", {"entities" : qUnion([Q0]), "operationType" : NewBodyOperationType.REMOVE, "oppositeDirection" : true, "depth" : 8 * mm, "offsetDistance" : 25 * mm});
        }
    });
